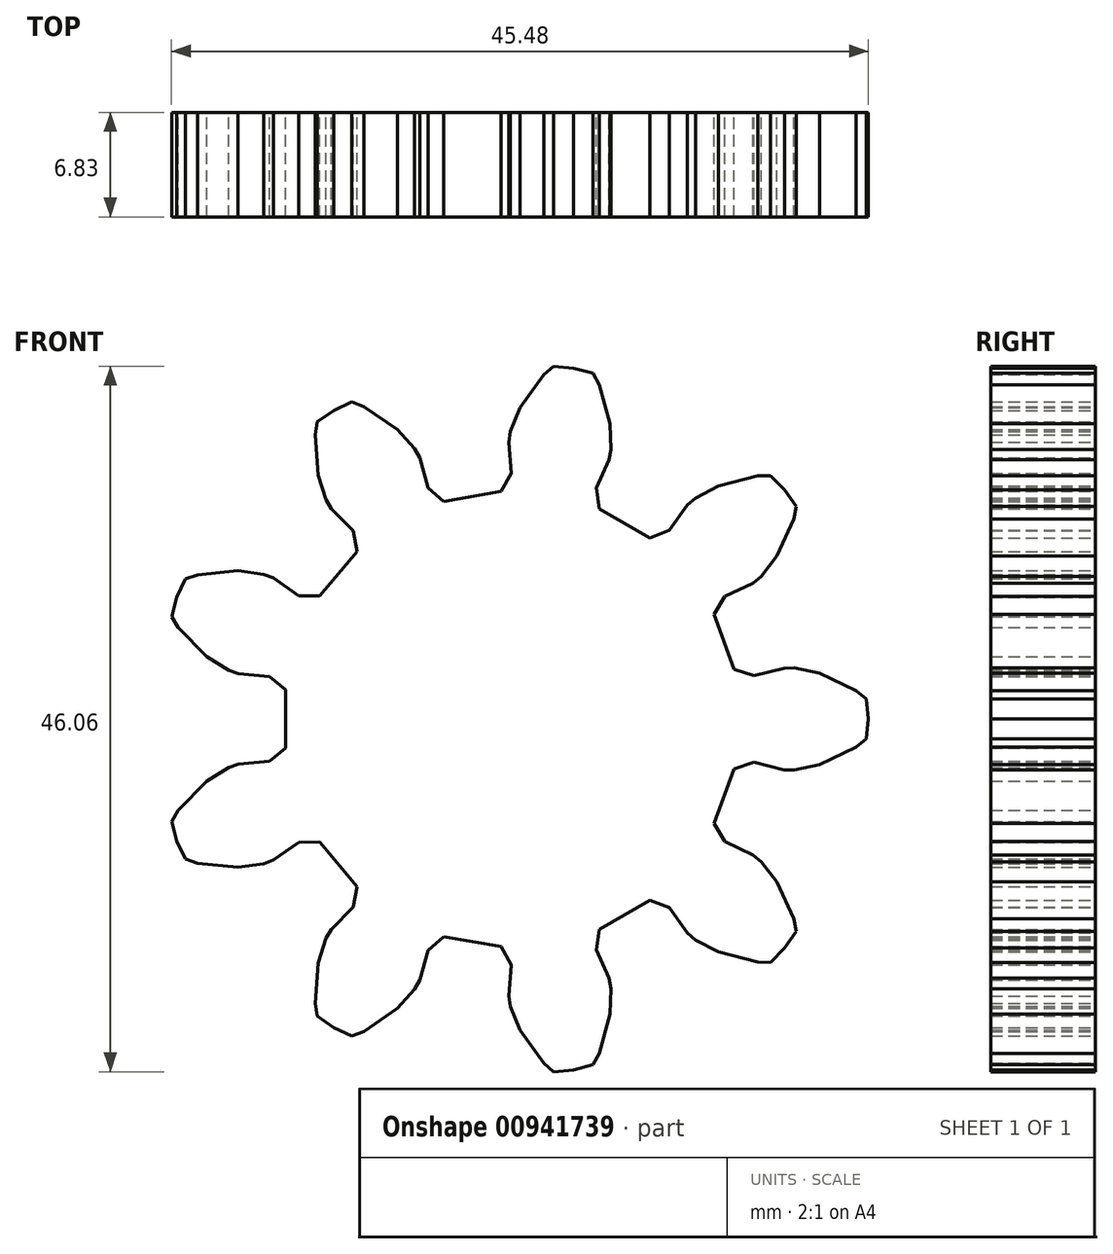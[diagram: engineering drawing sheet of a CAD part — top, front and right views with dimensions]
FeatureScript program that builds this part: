
annotation { "Feature Type Name" : "Feature", "Feature Type Description" : "" }
export const myFeature = defineFeature(function(context is Context, id is Id, definition is map)
    precondition{}
    {
        {
            var Q0;
            Q0=qCreatedBy(makeId("Front.planeOp"),FACE);
            var sketch = newSketch(context, id + "F0", { "sketchPlane" : qUnion([Q0])});
            skLineSegment(sketch, "E0", {"start": v(16.36, -15.88) * mm, "end": v(17.3, -14.96) * mm});
            skLineSegment(sketch, "E1", {"start": v(17.3, -14.96) * mm, "end": v(18.04, -13.88) * mm});
            skLineSegment(sketch, "E2", {"start": v(18.04, -13.88) * mm, "end": v(17.88, -13.05) * mm});
            skLineSegment(sketch, "E3", {"start": v(17.88, -13.05) * mm, "end": v(16.78, -10.63) * mm});
            skLineSegment(sketch, "E4", {"start": v(16.78, -10.63) * mm, "end": v(15.76, -9.31) * mm});
            skLineSegment(sketch, "E5", {"start": v(15.76, -9.31) * mm, "end": v(15.21, -8.87) * mm});
            skLineSegment(sketch, "E6", {"start": v(15.21, -8.87) * mm, "end": v(13.39, -8) * mm});
            skLineSegment(sketch, "E7", {"start": v(13.39, -8) * mm, "end": v(12.68, -6.83) * mm});
            skLineSegment(sketch, "E8", {"start": v(12.68, -6.83) * mm, "end": v(13.98, -3.26) * mm});
            skLineSegment(sketch, "E9", {"start": v(13.98, -3.26) * mm, "end": v(15.28, -2.82) * mm});
            skLineSegment(sketch, "E10", {"start": v(15.28, -2.82) * mm, "end": v(17.23, -3.32) * mm});
            skLineSegment(sketch, "E11", {"start": v(17.23, -3.32) * mm, "end": v(17.93, -3.34) * mm});
            skLineSegment(sketch, "E12", {"start": v(17.93, -3.34) * mm, "end": v(19.57, -2.98) * mm});
            skLineSegment(sketch, "E13", {"start": v(19.57, -2.98) * mm, "end": v(21.96, -1.84) * mm});
            skLineSegment(sketch, "E14", {"start": v(21.96, -1.84) * mm, "end": v(22.62, -1.3) * mm});
            skLineSegment(sketch, "E15", {"start": v(22.62, -1.3) * mm, "end": v(22.74, 0) * mm});
            skLineSegment(sketch, "E16", {"start": v(22.74, 0) * mm, "end": v(22.62, 1.3) * mm});
            skLineSegment(sketch, "E17", {"start": v(22.62, 1.3) * mm, "end": v(21.96, 1.84) * mm});
            skLineSegment(sketch, "E18", {"start": v(21.96, 1.84) * mm, "end": v(19.57, 2.98) * mm});
            skLineSegment(sketch, "E19", {"start": v(19.57, 2.98) * mm, "end": v(17.93, 3.34) * mm});
            skLineSegment(sketch, "E20", {"start": v(17.93, 3.34) * mm, "end": v(17.23, 3.32) * mm});
            skLineSegment(sketch, "E21", {"start": v(17.23, 3.32) * mm, "end": v(15.28, 2.82) * mm});
            skLineSegment(sketch, "E22", {"start": v(15.28, 2.82) * mm, "end": v(13.98, 3.26) * mm});
            skLineSegment(sketch, "E23", {"start": v(13.98, 3.26) * mm, "end": v(12.68, 6.83) * mm});
            skLineSegment(sketch, "E24", {"start": v(12.68, 6.83) * mm, "end": v(13.39, 8) * mm});
            skLineSegment(sketch, "E25", {"start": v(13.39, 8) * mm, "end": v(15.21, 8.87) * mm});
            skLineSegment(sketch, "E26", {"start": v(15.21, 8.87) * mm, "end": v(15.76, 9.31) * mm});
            skLineSegment(sketch, "E27", {"start": v(15.76, 9.31) * mm, "end": v(16.78, 10.63) * mm});
            skLineSegment(sketch, "E28", {"start": v(16.78, 10.63) * mm, "end": v(17.88, 13.05) * mm});
            skLineSegment(sketch, "E29", {"start": v(17.88, 13.05) * mm, "end": v(18.04, 13.88) * mm});
            skLineSegment(sketch, "E30", {"start": v(18.04, 13.88) * mm, "end": v(17.3, 14.96) * mm});
            skLineSegment(sketch, "E31", {"start": v(17.3, 14.96) * mm, "end": v(16.36, 15.88) * mm});
            skLineSegment(sketch, "E32", {"start": v(16.36, 15.88) * mm, "end": v(15.52, 15.87) * mm});
            skLineSegment(sketch, "E33", {"start": v(15.52, 15.87) * mm, "end": v(12.95, 15.2) * mm});
            skLineSegment(sketch, "E34", {"start": v(12.95, 15.2) * mm, "end": v(11.47, 14.42) * mm});
            skLineSegment(sketch, "E35", {"start": v(11.47, 14.42) * mm, "end": v(10.94, 13.97) * mm});
            skLineSegment(sketch, "E36", {"start": v(10.94, 13.97) * mm, "end": v(9.77, 12.32) * mm});
            skLineSegment(sketch, "E37", {"start": v(9.77, 12.32) * mm, "end": v(8.5, 11.83) * mm});
            skLineSegment(sketch, "E38", {"start": v(8.5, 11.83) * mm, "end": v(5.2, 13.73) * mm});
            skLineSegment(sketch, "E39", {"start": v(5.2, 13.73) * mm, "end": v(4.99, 15.08) * mm});
            skLineSegment(sketch, "E40", {"start": v(4.99, 15.08) * mm, "end": v(5.83, 16.92) * mm});
            skLineSegment(sketch, "E41", {"start": v(5.83, 16.92) * mm, "end": v(5.96, 17.6) * mm});
            skLineSegment(sketch, "E42", {"start": v(5.96, 17.6) * mm, "end": v(5.9, 19.28) * mm});
            skLineSegment(sketch, "E43", {"start": v(5.9, 19.28) * mm, "end": v(5.18, 21.83) * mm});
            skLineSegment(sketch, "E44", {"start": v(5.18, 21.83) * mm, "end": v(4.78, 22.57) * mm});
            skLineSegment(sketch, "E45", {"start": v(4.78, 22.57) * mm, "end": v(3.5, 22.91) * mm});
            skLineSegment(sketch, "E46", {"start": v(3.5, 22.91) * mm, "end": v(2.2, 23.03) * mm});
            skLineSegment(sketch, "E47", {"start": v(2.2, 23.03) * mm, "end": v(1.56, 22.47) * mm});
            skLineSegment(sketch, "E48", {"start": v(1.56, 22.47) * mm, "end": v(0.02, 20.31) * mm});
            skLineSegment(sketch, "E49", {"start": v(0.02, 20.31) * mm, "end": v(-0.61, 18.76) * mm});
            skLineSegment(sketch, "E50", {"start": v(-0.61, 18.76) * mm, "end": v(-0.72, 18.07) * mm});
            skLineSegment(sketch, "E51", {"start": v(-0.72, 18.07) * mm, "end": v(-0.56, 16.06) * mm});
            skLineSegment(sketch, "E52", {"start": v(-0.56, 16.06) * mm, "end": v(-1.22, 14.86) * mm});
            skLineSegment(sketch, "E53", {"start": v(-1.22, 14.86) * mm, "end": v(-4.97, 14.2) * mm});
            skLineSegment(sketch, "E54", {"start": v(-4.97, 14.2) * mm, "end": v(-6, 15.1) * mm});
            skLineSegment(sketch, "E55", {"start": v(-6, 15.1) * mm, "end": v(-6.54, 17.05) * mm});
            skLineSegment(sketch, "E56", {"start": v(-6.54, 17.05) * mm, "end": v(-6.87, 17.66) * mm});
            skLineSegment(sketch, "E57", {"start": v(-6.87, 17.66) * mm, "end": v(-8, 18.9) * mm});
            skLineSegment(sketch, "E58", {"start": v(-8, 18.9) * mm, "end": v(-10.19, 20.4) * mm});
            skLineSegment(sketch, "E59", {"start": v(-10.19, 20.4) * mm, "end": v(-10.98, 20.7) * mm});
            skLineSegment(sketch, "E60", {"start": v(-10.98, 20.7) * mm, "end": v(-12.17, 20.15) * mm});
            skLineSegment(sketch, "E61", {"start": v(-12.17, 20.15) * mm, "end": v(-13.24, 19.4) * mm});
            skLineSegment(sketch, "E62", {"start": v(-13.24, 19.4) * mm, "end": v(-13.37, 18.56) * mm});
            skLineSegment(sketch, "E63", {"start": v(-13.37, 18.56) * mm, "end": v(-13.16, 15.92) * mm});
            skLineSegment(sketch, "E64", {"start": v(-13.16, 15.92) * mm, "end": v(-12.65, 14.32) * mm});
            skLineSegment(sketch, "E65", {"start": v(-12.65, 14.32) * mm, "end": v(-12.3, 13.72) * mm});
            skLineSegment(sketch, "E66", {"start": v(-12.3, 13.72) * mm, "end": v(-10.88, 12.28) * mm});
            skLineSegment(sketch, "E67", {"start": v(-10.88, 12.28) * mm, "end": v(-10.61, 10.94) * mm});
            skLineSegment(sketch, "E68", {"start": v(-10.61, 10.94) * mm, "end": v(-13.06, 8.03) * mm});
            skLineSegment(sketch, "E69", {"start": v(-13.06, 8.03) * mm, "end": v(-14.42, 8.06) * mm});
            skLineSegment(sketch, "E70", {"start": v(-14.42, 8.06) * mm, "end": v(-16.09, 9.2) * mm});
            skLineSegment(sketch, "E71", {"start": v(-16.09, 9.2) * mm, "end": v(-16.74, 9.45) * mm});
            skLineSegment(sketch, "E72", {"start": v(-16.74, 9.45) * mm, "end": v(-18.4, 9.68) * mm});
            skLineSegment(sketch, "E73", {"start": v(-18.4, 9.68) * mm, "end": v(-21.04, 9.42) * mm});
            skLineSegment(sketch, "E74", {"start": v(-21.04, 9.42) * mm, "end": v(-21.84, 9.15) * mm});
            skLineSegment(sketch, "E75", {"start": v(-21.84, 9.15) * mm, "end": v(-22.4, 7.96) * mm});
            skLineSegment(sketch, "E76", {"start": v(-22.4, 7.96) * mm, "end": v(-22.74, 6.69) * mm});
            skLineSegment(sketch, "E77", {"start": v(-22.74, 6.69) * mm, "end": v(-22.3, 5.97) * mm});
            skLineSegment(sketch, "E78", {"start": v(-22.3, 5.97) * mm, "end": v(-20.44, 4.07) * mm});
            skLineSegment(sketch, "E79", {"start": v(-20.44, 4.07) * mm, "end": v(-19.02, 3.18) * mm});
            skLineSegment(sketch, "E80", {"start": v(-19.02, 3.18) * mm, "end": v(-18.36, 2.95) * mm});
            skLineSegment(sketch, "E81", {"start": v(-18.36, 2.95) * mm, "end": v(-16.35, 2.76) * mm});
            skLineSegment(sketch, "E82", {"start": v(-16.35, 2.76) * mm, "end": v(-15.29, 1.9) * mm});
            skLineSegment(sketch, "E83", {"start": v(-15.29, 1.9) * mm, "end": v(-15.29, -1.9) * mm});
            skLineSegment(sketch, "E84", {"start": v(-15.29, -1.9) * mm, "end": v(-16.35, -2.76) * mm});
            skLineSegment(sketch, "E85", {"start": v(-16.35, -2.76) * mm, "end": v(-18.36, -2.95) * mm});
            skLineSegment(sketch, "E86", {"start": v(-18.36, -2.95) * mm, "end": v(-19.02, -3.18) * mm});
            skLineSegment(sketch, "E87", {"start": v(-19.02, -3.18) * mm, "end": v(-20.44, -4.07) * mm});
            skLineSegment(sketch, "E88", {"start": v(-20.44, -4.07) * mm, "end": v(-22.3, -5.97) * mm});
            skLineSegment(sketch, "E89", {"start": v(-22.3, -5.97) * mm, "end": v(-22.74, -6.69) * mm});
            skLineSegment(sketch, "E90", {"start": v(-22.74, -6.69) * mm, "end": v(-22.4, -7.96) * mm});
            skLineSegment(sketch, "E91", {"start": v(-22.4, -7.96) * mm, "end": v(-21.84, -9.15) * mm});
            skLineSegment(sketch, "E92", {"start": v(-21.84, -9.15) * mm, "end": v(-21.04, -9.42) * mm});
            skLineSegment(sketch, "E93", {"start": v(-21.04, -9.42) * mm, "end": v(-18.4, -9.68) * mm});
            skLineSegment(sketch, "E94", {"start": v(-18.4, -9.68) * mm, "end": v(-16.74, -9.45) * mm});
            skLineSegment(sketch, "E95", {"start": v(-16.74, -9.45) * mm, "end": v(-16.09, -9.2) * mm});
            skLineSegment(sketch, "E96", {"start": v(-16.09, -9.2) * mm, "end": v(-14.42, -8.06) * mm});
            skLineSegment(sketch, "E97", {"start": v(-14.42, -8.06) * mm, "end": v(-13.06, -8.03) * mm});
            skLineSegment(sketch, "E98", {"start": v(-13.06, -8.03) * mm, "end": v(-10.61, -10.94) * mm});
            skLineSegment(sketch, "E99", {"start": v(-10.61, -10.94) * mm, "end": v(-10.88, -12.28) * mm});
            skLineSegment(sketch, "E100", {"start": v(-10.88, -12.28) * mm, "end": v(-12.3, -13.72) * mm});
            skLineSegment(sketch, "E101", {"start": v(-12.3, -13.72) * mm, "end": v(-12.65, -14.32) * mm});
            skLineSegment(sketch, "E102", {"start": v(-12.65, -14.32) * mm, "end": v(-13.16, -15.92) * mm});
            skLineSegment(sketch, "E103", {"start": v(-13.16, -15.92) * mm, "end": v(-13.37, -18.56) * mm});
            skLineSegment(sketch, "E104", {"start": v(-13.37, -18.56) * mm, "end": v(-13.24, -19.4) * mm});
            skLineSegment(sketch, "E105", {"start": v(-13.24, -19.4) * mm, "end": v(-12.17, -20.15) * mm});
            skLineSegment(sketch, "E106", {"start": v(-12.17, -20.15) * mm, "end": v(-10.98, -20.7) * mm});
            skLineSegment(sketch, "E107", {"start": v(-10.98, -20.7) * mm, "end": v(-10.19, -20.4) * mm});
            skLineSegment(sketch, "E108", {"start": v(-10.19, -20.4) * mm, "end": v(-8, -18.9) * mm});
            skLineSegment(sketch, "E109", {"start": v(-8, -18.9) * mm, "end": v(-6.87, -17.66) * mm});
            skLineSegment(sketch, "E110", {"start": v(-6.87, -17.66) * mm, "end": v(-6.54, -17.05) * mm});
            skLineSegment(sketch, "E111", {"start": v(-6.54, -17.05) * mm, "end": v(-6, -15.1) * mm});
            skLineSegment(sketch, "E112", {"start": v(-6, -15.1) * mm, "end": v(-4.97, -14.2) * mm});
            skLineSegment(sketch, "E113", {"start": v(-4.97, -14.2) * mm, "end": v(-1.22, -14.86) * mm});
            skLineSegment(sketch, "E114", {"start": v(-1.22, -14.86) * mm, "end": v(-0.56, -16.06) * mm});
            skLineSegment(sketch, "E115", {"start": v(-0.56, -16.06) * mm, "end": v(-0.72, -18.07) * mm});
            skLineSegment(sketch, "E116", {"start": v(-0.72, -18.07) * mm, "end": v(-0.61, -18.76) * mm});
            skLineSegment(sketch, "E117", {"start": v(-0.61, -18.76) * mm, "end": v(0.02, -20.31) * mm});
            skLineSegment(sketch, "E118", {"start": v(0.02, -20.31) * mm, "end": v(1.56, -22.47) * mm});
            skLineSegment(sketch, "E119", {"start": v(1.56, -22.47) * mm, "end": v(2.2, -23.03) * mm});
            skLineSegment(sketch, "E120", {"start": v(2.2, -23.03) * mm, "end": v(3.5, -22.91) * mm});
            skLineSegment(sketch, "E121", {"start": v(3.5, -22.91) * mm, "end": v(4.78, -22.57) * mm});
            skLineSegment(sketch, "E122", {"start": v(4.78, -22.57) * mm, "end": v(5.18, -21.83) * mm});
            skLineSegment(sketch, "E123", {"start": v(5.18, -21.83) * mm, "end": v(5.9, -19.28) * mm});
            skLineSegment(sketch, "E124", {"start": v(5.9, -19.28) * mm, "end": v(5.96, -17.6) * mm});
            skLineSegment(sketch, "E125", {"start": v(5.96, -17.6) * mm, "end": v(5.83, -16.92) * mm});
            skLineSegment(sketch, "E126", {"start": v(5.83, -16.92) * mm, "end": v(4.99, -15.08) * mm});
            skLineSegment(sketch, "E127", {"start": v(4.99, -15.08) * mm, "end": v(5.2, -13.73) * mm});
            skLineSegment(sketch, "E128", {"start": v(5.2, -13.73) * mm, "end": v(8.5, -11.83) * mm});
            skLineSegment(sketch, "E129", {"start": v(8.5, -11.83) * mm, "end": v(9.77, -12.32) * mm});
            skLineSegment(sketch, "E130", {"start": v(9.77, -12.32) * mm, "end": v(10.94, -13.97) * mm});
            skLineSegment(sketch, "E131", {"start": v(10.94, -13.97) * mm, "end": v(11.47, -14.42) * mm});
            skLineSegment(sketch, "E132", {"start": v(11.47, -14.42) * mm, "end": v(12.95, -15.2) * mm});
            skLineSegment(sketch, "E133", {"start": v(12.95, -15.2) * mm, "end": v(15.52, -15.87) * mm});
            skLineSegment(sketch, "E134", {"start": v(15.52, -15.87) * mm, "end": v(16.36, -15.88) * mm});
            skSolve(sketch);
        }
        {
            var Q0;
            Q0=makeQuery(id+"F0.imprint","IMPRINT",FACE,{"disambiguationData":[TD([[makeQuery(id+"F0.imprint","IMPRINT",EDGE,{"derivedFrom":sQuery(id+"F0.wireOp",EDGE,"E0")}),1.0]])]});
            extrude(context, id + "F1", {"entities" : qUnion([Q0]), "depth" : 6.83 * mm, "offsetDistance" : 25 * mm});
        }
    });
